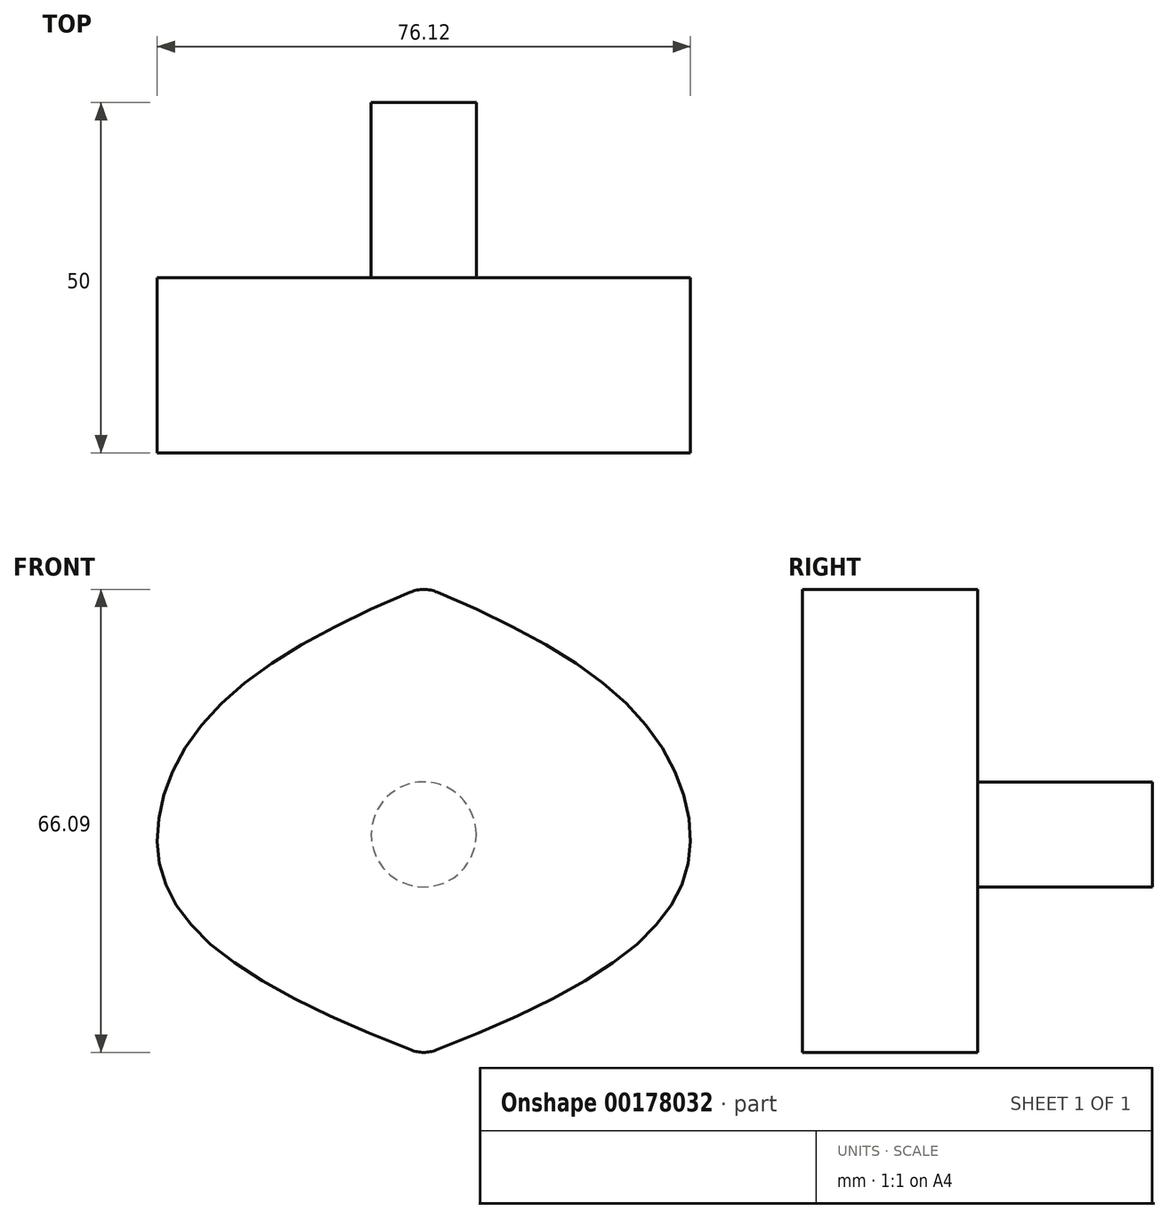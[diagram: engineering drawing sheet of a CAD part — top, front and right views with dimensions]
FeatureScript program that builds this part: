
annotation { "Feature Type Name" : "Feature", "Feature Type Description" : "" }
export const myFeature = defineFeature(function(context is Context, id is Id, definition is map)
    precondition{}
    {
        {
            var Q0;
            Q0=qCreatedBy(makeId("Front.planeOp"),FACE);
            var sketch = newSketch(context, id + "F0", { "sketchPlane" : qUnion([Q0])});
            skFitSpline(sketch, "E0", {"points": [v(0, 35.39) * mm, v(-31, 16.47) * mm, v(-38.05, 0) * mm, v(-32.97, -13.2) * mm, v(0, -31.47) * mm], "startDerivative": vector(-139.41, -56.83) * mm, "endDerivative": vector(150, -56.78) * mm});
            skLineSegment(sketch, "E1", {"start": v(0, 35.39) * mm, "end": v(0, -31.47) * mm, "construction": true});
            skFitSpline(sketch, "E2.MirrorCS", {"points": [v(0, 35.39) * mm, v(31, 16.47) * mm, v(38.05, 0) * mm, v(32.97, -13.2) * mm, v(0, -31.47) * mm], "startDerivative": vector(139.41, -56.83) * mm, "endDerivative": vector(-150, -56.78) * mm});
            skSolve(sketch);
        }
        {
            var Q0;
            Q0 = qSketchRegion(id + "F0", true);
            extrude(context, id + "F1", {"entities" : qUnion([Q0]), "depth" : 25 * mm});
        }
        {
            var Q0;
            Q0=makeQuery(id+"F1.opExtrude","CAP_FACE",FACE,{"disambiguationData":[OSD([sQuery(id+"F0.wireOp",EDGE,"E0"),sQuery(id+"F0.wireOp",EDGE,"E2.MirrorCS")])],"isStart":true});
            var sketch = newSketch(context, id + "F2", { "sketchPlane" : qUnion([Q0])});
            skCircle(sketch, "E3", {"center": v(0, 0) * mm, "radius": 7.5 * mm});
            skSolve(sketch);
        }
        {
            var Q0;
            Q0 = qSketchRegion(id + "F2", true);
            extrude(context, id + "F3", {"entities" : qUnion([Q0]), "operationType" : NewBodyOperationType.ADD, "depth" : 25 * mm});
        }
        {
            var Q0;
            {var subQ0=sQuery(id+"F0.wireOp",EDGE,"E2.MirrorCS");var subQ1=sQuery(id+"F0.wireOp",EDGE,"E0");Q0=makeQuery(id+"F1.opExtrude","SWEPT_EDGE",EDGE,{"disambiguationData":[OSD([subQ1,subQ0]),TDD([makeQuery(id+"F0.imprint","INTERSECT",VERTEX,{"disambiguationData":[OD(0.0)],"derivedFrom":[subQ1,subQ0]})])]});}
            var Q1;
            {var subQ0=sQuery(id+"F0.wireOp",EDGE,"E2.MirrorCS");var subQ1=sQuery(id+"F0.wireOp",EDGE,"E0");Q1=makeQuery(id+"F1.opExtrude","SWEPT_EDGE",EDGE,{"disambiguationData":[OSD([subQ1,subQ0]),TDD([makeQuery(id+"F0.imprint","INTERSECT",VERTEX,{"disambiguationData":[OD(1.0)],"derivedFrom":[subQ1,subQ0]})])]});}
            fillet(context, id + "F4", {"entities" : qUnion([Q0, Q1]), "radius" : 5 * mm, "tangentPropagation" : true, "allowEdgeOverflow" : false});
        }
    });
